annotation { "Feature Type Name" : "Feature", "Feature Type Description" : "" }
export const myFeature = defineFeature(function(context is Context, id is Id, definition is map)
    precondition{}
    {
        {
            var Q0;
            Q0=qCreatedBy(makeId("Front.planeOp"),FACE);
            var sketch = newSketch(context, id + "F0", { "sketchPlane" : qUnion([Q0])});
            skArc(sketch, "E0", {"start": v(-5.7, 10.47) * mm, "mid": v(-7.9, 5.34) * mm, "end": v(-9.54, 0) * mm});
            skArc(sketch, "E1", {"start": v(6.43, 15.65) * mm, "mid": v(0.23, 13.37) * mm, "end": v(-5.7, 10.47) * mm});
            skArc(sketch, "E2", {"start": v(19.54, 11.81) * mm, "mid": v(13.1, 14.13) * mm, "end": v(6.43, 15.65) * mm});
            skArc(sketch, "E3", {"start": v(26.25, 1.68) * mm, "mid": v(23.23, 6.97) * mm, "end": v(19.54, 11.81) * mm});
            skArc(sketch, "E4", {"start": v(26.25, 0) * mm, "mid": v(26.31, 0.84) * mm, "end": v(26.25, 1.68) * mm});
            skLineSegment(sketch, "E5", {"start": v(-9.54, 0) * mm, "end": v(26.25, 0) * mm});
            skLineSegment(sketch, "E6", {"start": v(-74.27, 0) * mm, "end": v(26.23, 0) * mm, "construction": true});
            skSolve(sketch);
        }
        {
            var Q0;
            Q0 = qSketchRegion(id + "F0", true);
            var Q1;
            Q1=sQuery(id+"F0.wireOp",EDGE,"E6");
            revolve(context, id + "F1", {"entities" : qUnion([Q0]), "axis" : qUnion([Q1]), "revolveType" : RevolveType.FULL});
        }
        {
            var Q0;
            Q0=qCreatedBy(makeId("Front.planeOp"),FACE);
            var sketch = newSketch(context, id + "F2", { "sketchPlane" : qUnion([Q0])});
            skLineSegment(sketch, "E7", {"start": v(28.23, 1.69) * mm, "end": v(28.23, 0.06) * mm});
            skLineSegment(sketch, "E8", {"start": v(25.6, 0) * mm, "end": v(28.23, 0) * mm});
            skPoint(sketch, "E9.orphan", {"position": v(28.23, -2.24) * mm});
            skLineSegment(sketch, "E10", {"start": v(22.9, 0) * mm, "end": v(25.6, 0) * mm, "construction": true});
            skPoint(sketch, "E11.visualSharp", {"position": v(28.23, 2.24) * mm});
            skArc(sketch, "E11.filletArc", {"start": v(28.23, 1.69) * mm, "mid": v(28.08, 1.92) * mm, "end": v(27.8, 1.88) * mm});
            skLineSegment(sketch, "E12", {"start": v(25.6, 0.06) * mm, "end": v(25.6, 0.2) * mm});
            skLineSegment(sketch, "E13", {"start": v(25.6, 0.2) * mm, "end": v(27.8, 1.88) * mm});
            skLineSegment(sketch, "E14", {"start": v(25.6, 0.06) * mm, "end": v(28.23, 0.06) * mm});
            skLineSegment(sketch, "E15.trimOffspring", {"start": v(28.23, 0) * mm, "end": v(30.76, 0) * mm, "construction": true});
            skSolve(sketch);
        }
        {
            var Q0;
            Q0=makeQuery(id+"F2.imprint","IMPRINT",FACE,{"disambiguationData":[TD([[makeQuery(id+"F2.imprint","IMPRINT",EDGE,{"derivedFrom":sQuery(id+"F2.wireOp",EDGE,"E7")}),-1.0]])]});
            var Q1;
            Q1=sQuery(id+"F2.wireOp",EDGE,"E10");
            revolve(context, id + "F3", {"operationType" : NewBodyOperationType.ADD, "entities" : qUnion([Q0]), "axis" : qUnion([Q1]), "revolveType" : RevolveType.FULL});
        }
        {
            var Q0;
            Q0=qCreatedBy(makeId("Front.planeOp"),FACE);
            var sketch = newSketch(context, id + "F4", { "sketchPlane" : qUnion([Q0])});
            skLineSegment(sketch, "E16", {"start": v(25.66, 0.05) * mm, "end": v(28.23, 1.69) * mm});
            skLineSegment(sketch, "E17", {"start": v(28.22, 0.06) * mm, "end": v(25.66, 0.05) * mm});
            skPoint(sketch, "E18.orphan", {"position": v(25.58, 0) * mm});
            skLineSegment(sketch, "E19", {"start": v(28.23, 1.69) * mm, "end": v(28.23, 0.06) * mm});
            skLineSegment(sketch, "E20", {"start": v(28.23, 0.06) * mm, "end": v(28.22, 0.06) * mm});
            skLineSegment(sketch, "E21", {"start": v(28.3, 0.06) * mm, "end": v(25.54, 0.05) * mm, "construction": true});
            skSolve(sketch);
        }
        {
            var Q0;
            Q0 = qSketchRegion(id + "F4", true);
            var Q1;
            Q1=sQuery(id+"F4.wireOp",EDGE,"E21");
            revolve(context, id + "F5", {"operationType" : NewBodyOperationType.REMOVE, "entities" : qUnion([Q0]), "axis" : qUnion([Q1]), "revolveType" : RevolveType.FULL});
        }
    });